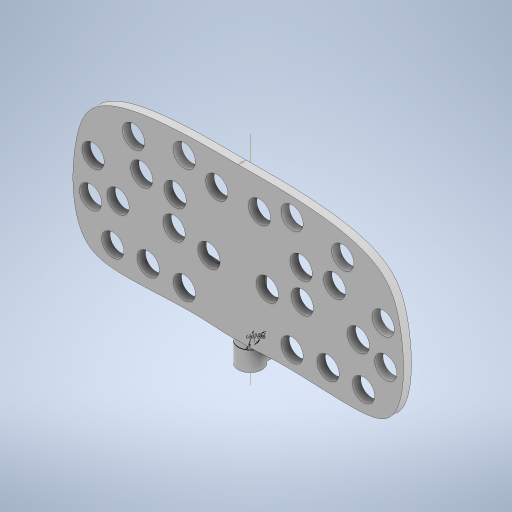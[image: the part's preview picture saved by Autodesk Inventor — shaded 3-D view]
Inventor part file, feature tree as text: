
AUTODESK INVENTOR PART (.ipt)
format: ipt  version: 2023 (Build 270158000, 158)  size: 1,217,536 bytes
history: native  units: in
note: dims shown in document units (in); Inventor stores cm internally (conversion verified against a paired STEP export)
features: extrude x14, sketch x9, plane x5, sweep x4, mirror x1, split x1, fillet x1, projected_geometry x1
ambient origin geometry x8: Origin, YZ Plane, XZ Plane, XY Plane, X Axis, Y Axis, Z Axis, Center Point
bodies: Solid1 (feature_tree)
feature tree (36):
  plane  "Work Plane5"
  extrude  "Extrusion1"  Depth=0.4724in
  sketch  "Sketch3"  dims[d0=0.3228in d1=0.4724in]
  sketch  "Sketch9"  dims[d13=-0.0186in d14=0.0in d15=-0.0206in d16=0.0in]
  plane  "Work Plane6"
  sketch  "Sketch10"  dims[d17=1.6142in d18=0.0in d19=0.1181in d20=0.0in]
  sweep  "Sweep1"
  sweep  "Sweep2"
  sweep  "Sweep3"
  extrude  "Extrusion3"  Depth=0.5118in
  extrude  "Extrusion4"  Depth=0.5118in
  extrude  "Extrusion5"  Depth=0.5118in
  extrude  "Extrusion6"  Depth=0.5118in
  sketch  "Sketch11"  dims[d22=0.1575in d23=0.0in d52=0.5118in]
  extrude  "Extrusion14"  Depth=0.0394in
  extrude  "Extrusion8"  Depth=0.0394in
  sketch  "Sketch12"  dims[d54=0.5118in d55=0.5118in]
  sweep  "Sweep4"
  plane  "Work Plane1"
  mirror  "Mirror2"
  plane  "Work Plane2"
  plane  "Work Plane3"
  split  "Split4"
  extrude  "Extrusion15"  Depth=0.0394in
  sketch  "Sketch14"  dims[d60=0.5118in d62=0.5118in]
  extrude  "Extrusion16"  Depth=0.0394in TaperAngle=0.0deg
  extrude  "Extrusion17"  Depth=1.6142in TaperAngle=0.0deg
  extrude  "Extrusion18"  [1 undecoded]
  sketch  "Sketch15"  dims[d65=0.5118in d66=0.5118in d67=0.5118in d68=0.5118in d69=0.5118in d70=0.1575in d71=0.0in d92=1.6142in d93=0.0in d94=-0.3937in d121=0.3125in d122=-0.3125in d124=0.5118in d125=0.0787in d139=0.1969in d140=0.0137in d142=-0.055in d143=0.0in d144=0.3937in d145=0.0in d146=0.0787in d147=0.0787in d148=0.0984in d149=0.0in d150=0.4724in d151=0.0in d152=0.2165in d153=0.0787in d154=0.0in d155=0.0in d156=0.315in d157=0.0in d158=0.1378in d159=0.2362in d160=0.2165in d161=0.315in d162=0.0in d163=0.0394in d164=0.0in d165=0.0394in d166=0.0in d167=0.0394in d141=0.1969in]
  extrude  "Extrusion19"  Depth=0.0394in
  extrude  "Extrusion20"  Depth=0.0394in
  extrude  "Extrusion21"  Depth=0.0787in
  fillet  "Fillet2"  Radius=0.1969in
  sketch  "Sketch4"  dims[d2=1.6142in d3=0.0in d11=-0.0192in d12=0.0in]
  sketch  "Sketch13"  dims[d57=0.5118in d59=0.5118in]
  projected_geometry  "Projected Loop27"
note: 1 required parameter value undecoded (feature->parameter linkage not recoverable at this tier; creation-order binding heuristic only, values carry confidence <= 0.55)
